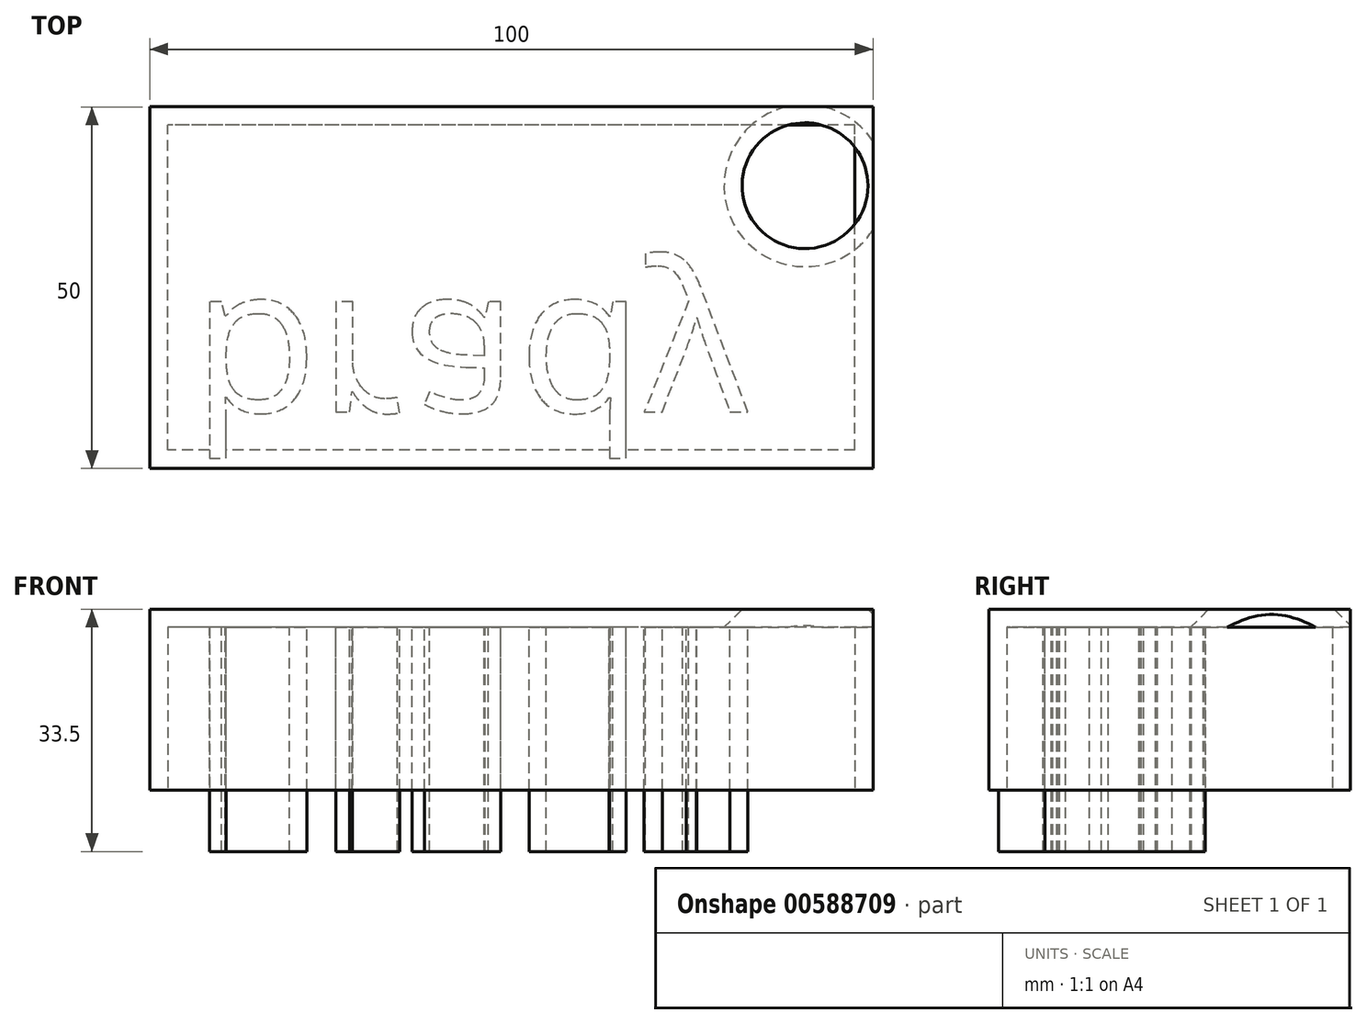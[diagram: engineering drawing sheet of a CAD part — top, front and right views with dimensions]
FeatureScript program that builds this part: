
annotation { "Feature Type Name" : "Feature", "Feature Type Description" : "" }
export const myFeature = defineFeature(function(context is Context, id is Id, definition is map)
    precondition{}
    {
        {
            var Q0;
            Q0=qCreatedBy(makeId("Top.planeOp"),FACE);
            var sketch = newSketch(context, id + "F0", { "sketchPlane" : qUnion([Q0])});
            skLineSegment(sketch, "E0.bottom", {"start": v(0, 16.43) * mm, "end": v(-100, 16.43) * mm});
            skLineSegment(sketch, "E0.top", {"start": v(0, 66.43) * mm, "end": v(-100, 66.43) * mm});
            skLineSegment(sketch, "E0.left", {"start": v(0, 16.43) * mm, "end": v(0, 66.43) * mm});
            skLineSegment(sketch, "E0.right", {"start": v(-100, 16.43) * mm, "end": v(-100, 66.43) * mm});
            skPoint(sketch, "E0.middle", {"position": v(-50, 41.43) * mm});
            skSolve(sketch);
        }
        {
            var Q0;
            Q0=makeQuery(id+"F0.imprint","IMPRINT",FACE,{"disambiguationData":[TD([[makeQuery(id+"F0.imprint","IMPRINT",EDGE,{"derivedFrom":sQuery(id+"F0.wireOp",EDGE,"E0.bottom")}),-1.0]])]});
            extrude(context, id + "F1", {"entities" : qUnion([Q0]), "depth" : 25 * mm, "offsetDistance" : 25 * mm});
        }
        {
            var Q0;
            Q0=makeQuery(id+"F1.opExtrude","CAP_FACE",FACE,{"disambiguationData":[OSD([sQuery(id+"F0.wireOp",EDGE,"E0.bottom"),sQuery(id+"F0.wireOp",EDGE,"E0.top"),sQuery(id+"F0.wireOp",EDGE,"E0.left"),sQuery(id+"F0.wireOp",EDGE,"E0.right")])],"isStart":true});
            shell(context, id + "F2", {"entities" : qUnion([Q0]), "thickness" : 2.5 * mm});
        }
        {
            var Q0;
            Q0=makeQuery(id+"F2.opShell","OFFSET_FACE",FACE,{"disambiguationData":[OSD([sQuery(id+"F0.wireOp",EDGE,"E0.bottom"),sQuery(id+"F0.wireOp",EDGE,"E0.top"),sQuery(id+"F0.wireOp",EDGE,"E0.left"),sQuery(id+"F0.wireOp",EDGE,"E0.right")])]});
            var sketch = newSketch(context, id + "F3", { "sketchPlane" : qUnion([Q0])});
            skCircle(sketch, "E1", {"center": v(-9.4, -55.52) * mm, "radius": 8.04 * mm});
            skSolve(sketch);
        }
        {
            var Q0;
            Q0=sQuery(id+"F3.wireOp",VERTEX,"E1.center");
            var Q1;
            Q1=makeQuery(id+"F1.opExtrude","SWEPT_BODY",BODY,{"disambiguationData":[OSD([sQuery(id+"F0.wireOp",EDGE,"E0.bottom"),sQuery(id+"F0.wireOp",EDGE,"E0.top"),sQuery(id+"F0.wireOp",EDGE,"E0.left"),sQuery(id+"F0.wireOp",EDGE,"E0.right")])]});
            hole(context, id + "F4", {"style" : HoleStyle.C_SINK, "endStyle" : HoleEndStyle.BLIND, "standardTappedOrClearance" : lookupTablePath({ "standard" : "ISO", "fit" : "Normal", "size" : "M10", "type" : "Clearance" }), "standardBlindInLast" : lookupTablePath({ "fit" : "Standard", "standard" : "ISO", "size" : "M10", "type" : "Clearance" }), "holeDiameter" : 11 * mm, "cSinkDiameter" : 22.4 * mm, "cSinkAngle" : 90 * degree, "majorDiameter" : 5 * mm, "holeDepth" : 12 * mm, "isTappedThrough" : true, "tappedDepth" : 12 * mm, "tapClearance" : 3, "locations" : qUnion([Q0]), "scope" : qUnion([Q1])});
        }
        {
            var Q0;
            Q0=makeQuery(id+"F2.opShell","OFFSET_FACE",FACE,{"disambiguationData":[OSD([sQuery(id+"F0.wireOp",EDGE,"E0.bottom"),sQuery(id+"F0.wireOp",EDGE,"E0.top"),sQuery(id+"F0.wireOp",EDGE,"E0.left"),sQuery(id+"F0.wireOp",EDGE,"E0.right")])]});
            var sketch = newSketch(context, id + "F5", { "sketchPlane" : qUnion([Q0])});
            skText(sketch, "E2", { "text": "brady", "fontName": "OpenSans-Regular.ttf"});
            const initialGuessF5  = {"E2": [-0.09421, -0.0395, 1, 0, 0.02056]};
            skSetInitialGuess(sketch, initialGuessF5);
            skSolve(sketch);
        }
        {
            var Q0;
            Q0 = qSketchRegion(id + "F5", true);
            extrude(context, id + "F6", {"entities" : qUnion([Q0]), "operationType" : NewBodyOperationType.ADD, "depth" : 31 * mm, "offsetDistance" : 25 * mm});
        }
    });
